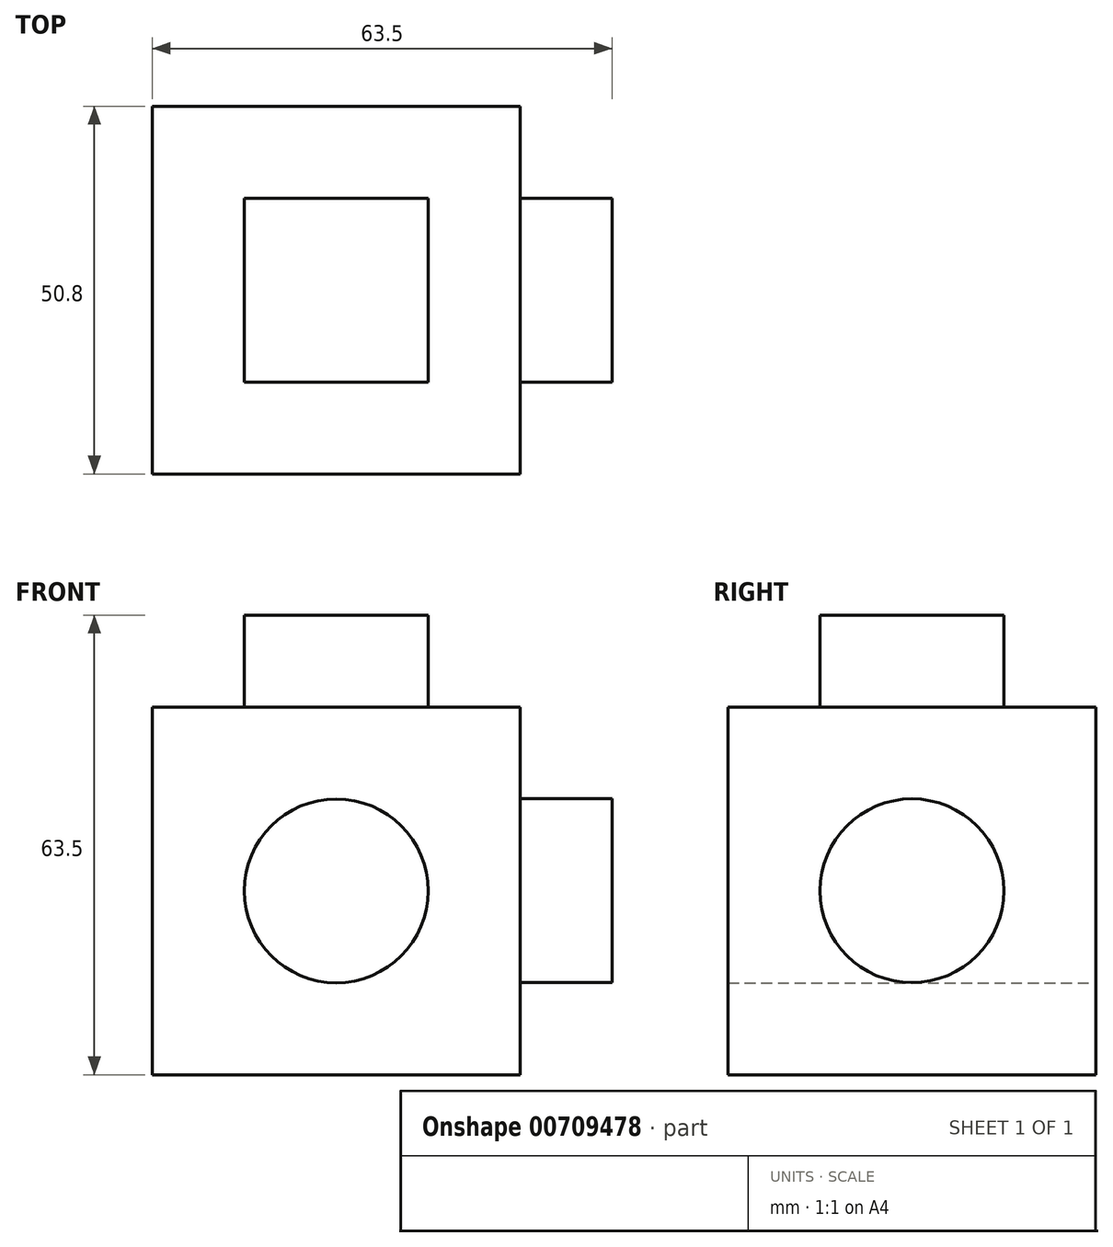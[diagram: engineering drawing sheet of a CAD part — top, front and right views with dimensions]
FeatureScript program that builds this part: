
annotation { "Feature Type Name" : "Feature", "Feature Type Description" : "" }
export const myFeature = defineFeature(function(context is Context, id is Id, definition is map)
    precondition{}
    {
        {
            var Q0;
            Q0=qCreatedBy(makeId("Front.planeOp"),FACE);
            var sketch = newSketch(context, id + "F0", { "sketchPlane" : qUnion([Q0])});
            skLineSegment(sketch, "E0.bottom", {"start": v(0, 0) * mm, "end": v(-50.8, 0) * mm});
            skLineSegment(sketch, "E0.top", {"start": v(0, 50.8) * mm, "end": v(-50.8, 50.8) * mm});
            skLineSegment(sketch, "E0.left", {"start": v(0, 0) * mm, "end": v(0, 50.8) * mm});
            skLineSegment(sketch, "E0.right", {"start": v(-50.8, 0) * mm, "end": v(-50.8, 50.8) * mm});
            skCircle(sketch, "E1", {"center": v(-25.4, 25.4) * mm, "radius": 12.7 * mm});
            skSolve(sketch);
        }
        {
            var Q0;
            Q0 = qSketchRegion(id + "F0", true);
            extrude(context, id + "F1", {"entities" : qUnion([Q0]), "depth" : 50.8 * mm, "offsetDistance" : 25.4 * mm});
        }
        {
            var Q0;
            Q0=makeQuery(id+"F1.opExtrude","SWEPT_FACE",FACE,{"disambiguationData":[OSD([sQuery(id+"F0.wireOp",EDGE,"E0.top")])]});
            var sketch = newSketch(context, id + "F2", { "sketchPlane" : qUnion([Q0])});
            skLineSegment(sketch, "E2.bottom", {"start": v(-38.1, -12.7) * mm, "end": v(-12.7, -12.7) * mm});
            skLineSegment(sketch, "E2.top", {"start": v(-38.1, -38.1) * mm, "end": v(-12.7, -38.1) * mm});
            skLineSegment(sketch, "E2.left", {"start": v(-38.1, -12.7) * mm, "end": v(-38.1, -38.1) * mm});
            skLineSegment(sketch, "E2.right", {"start": v(-12.7, -12.7) * mm, "end": v(-12.7, -38.1) * mm});
            skSolve(sketch);
        }
        {
            var Q0;
            Q0 = qSketchRegion(id + "F2", true);
            extrude(context, id + "F3", {"entities" : qUnion([Q0]), "operationType" : NewBodyOperationType.ADD, "depth" : 12.7 * mm, "offsetDistance" : 25.4 * mm});
        }
        {
            var Q0;
            Q0=makeQuery(id+"F1.opExtrude","SWEPT_FACE",FACE,{"disambiguationData":[OSD([sQuery(id+"F0.wireOp",EDGE,"E0.left")])]});
            var sketch = newSketch(context, id + "F4", { "sketchPlane" : qUnion([Q0])});
            skCircle(sketch, "E3", {"center": v(-25.4, 25.4) * mm, "radius": 12.7 * mm});
            skSolve(sketch);
        }
        {
            var Q0;
            Q0 = qSketchRegion(id + "F4", true);
            extrude(context, id + "F5", {"entities" : qUnion([Q0]), "operationType" : NewBodyOperationType.ADD, "depth" : 12.7 * mm, "offsetDistance" : 25.4 * mm});
        }
    });
